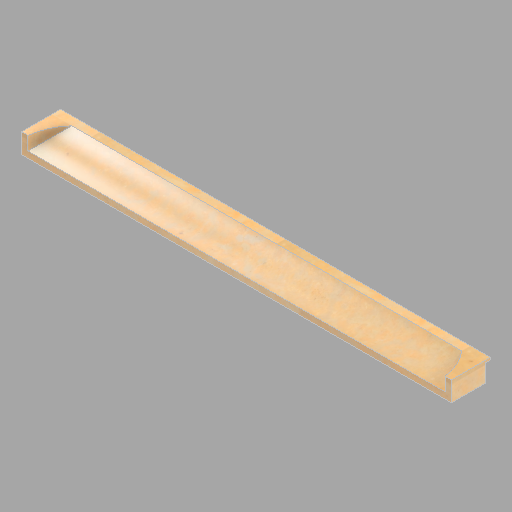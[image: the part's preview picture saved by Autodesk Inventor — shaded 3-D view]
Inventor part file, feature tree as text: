
AUTODESK INVENTOR PART (.ipt)
format: ipt  version: 2022.2 (Build 262287010, 287A)  size: 191,488 bytes
history: native  units: in
note: dims shown in document units (in); Inventor stores cm internally (conversion verified against a paired STEP export)
features: revolve x2, direct_edit x1
ambient origin geometry x8: Origin, YZ Plane, XZ Plane, XY Plane, X Axis, Y Axis, Z Axis, Center Point
bodies: Solid1 (feature_tree), Body1 (feature_tree)
feature tree (3):
  direct_edit  "Direct Edit1"
  revolve  "Rotate1"  [1 undecoded]
  revolve  "Rotate2"  Angle=180.0deg
note: 1 required parameter value undecoded (feature->parameter linkage not recoverable at this tier; creation-order binding heuristic only, values carry confidence <= 0.55)
